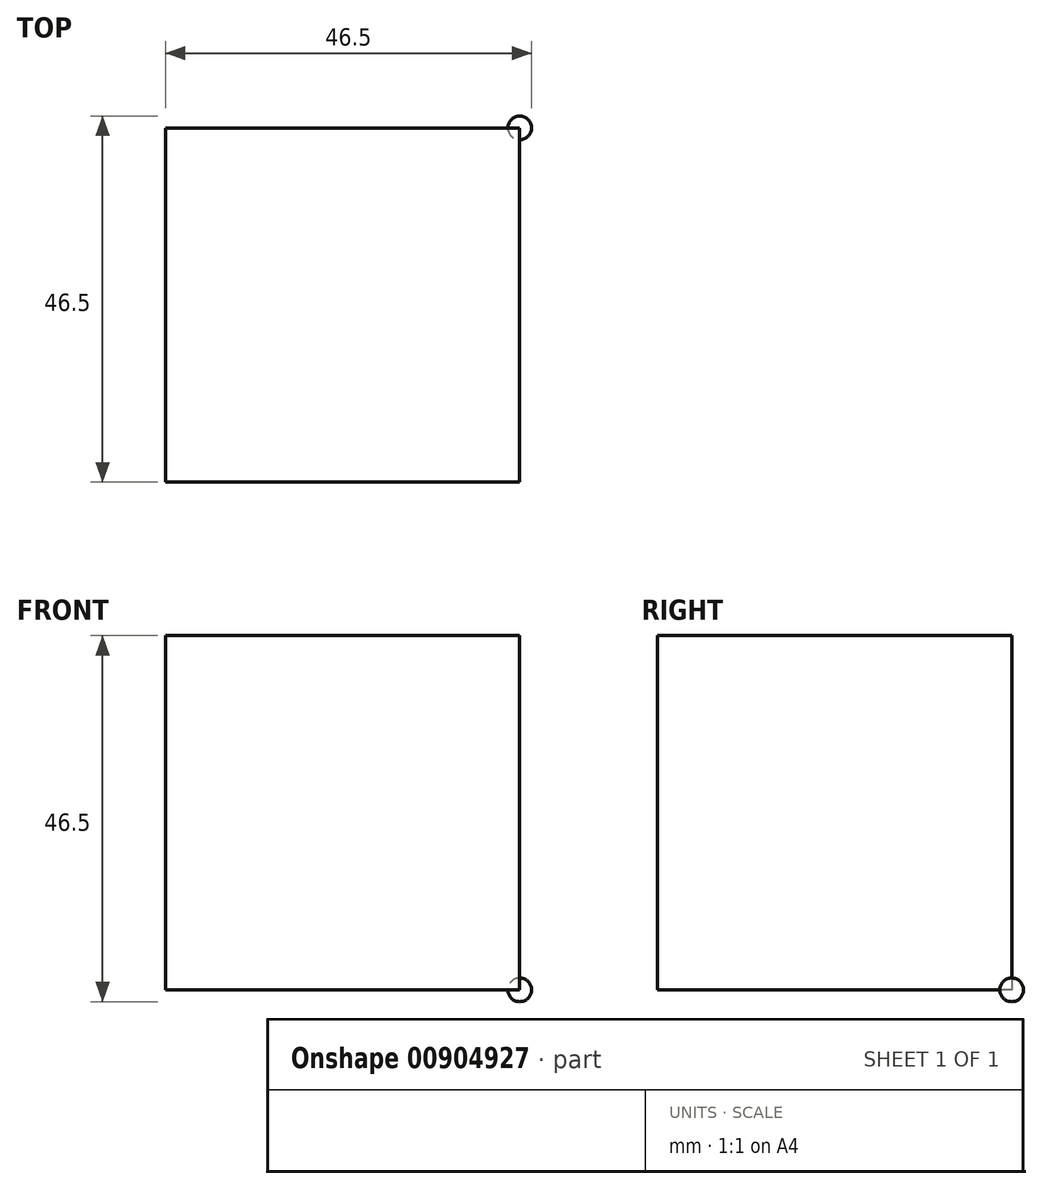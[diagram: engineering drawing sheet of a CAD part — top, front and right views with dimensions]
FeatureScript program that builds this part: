
annotation { "Feature Type Name" : "Feature", "Feature Type Description" : "" }
export const myFeature = defineFeature(function(context is Context, id is Id, definition is map)
    precondition{}
    {
        {
            var Q0;
            Q0=qCreatedBy(makeId("Top.planeOp"),FACE);
            var sketch = newSketch(context, id + "F0", { "sketchPlane" : qUnion([Q0])});
            skLineSegment(sketch, "E0.bottom", {"start": v(-22.5, 22.5) * mm, "end": v(22.5, 22.5) * mm});
            skLineSegment(sketch, "E0.top", {"start": v(-22.5, -22.5) * mm, "end": v(22.5, -22.5) * mm});
            skLineSegment(sketch, "E0.left", {"start": v(-22.5, 22.5) * mm, "end": v(-22.5, -22.5) * mm});
            skLineSegment(sketch, "E0.right", {"start": v(22.5, 22.5) * mm, "end": v(22.5, -22.5) * mm});
            skPoint(sketch, "E0.middle", {"position": v(0, 0) * mm});
            skArc(sketch, "E1", {"start": v(24, 22.5) * mm, "mid": v(22.5, 24) * mm, "end": v(21, 22.5) * mm});
            skCircle(sketch, "E2", {"center": v(22.5, -22.5) * mm, "radius": 1.5 * mm});
            skCircle(sketch, "E3", {"center": v(-22.5, 22.5) * mm, "radius": 1.5 * mm});
            skCircle(sketch, "E4", {"center": v(-22.5, -22.5) * mm, "radius": 1.5 * mm});
            skLineSegment(sketch, "E5", {"start": v(22.5, 22.5) * mm, "end": v(24, 22.5) * mm});
            skSolve(sketch);
        }
        {
            var Q0;
            {var subQ5=sQuery(id+"F0.wireOp",EDGE,"E3");var subQ13=sQuery(id+"F0.wireOp",EDGE,"E0.bottom");var subQ14=makeQuery(id+"F0.imprint","INTERSECT",VERTEX,{"derivedFrom":[subQ13,subQ5]});Q0=makeQuery(id+"F0.imprint","IMPRINT",FACE,{"disambiguationData":[TD([[makeQuery(id+"F0.imprint","IMPRINT",EDGE,{"disambiguationData":[TD([[subQ14,-1.0]])],"derivedFrom":subQ13}),-1.0]])]});}
            var Q1;
            {var subQ0=sQuery(id+"F0.wireOp",EDGE,"E0.right");var subQ1=sQuery(id+"F0.wireOp",EDGE,"E0.bottom");var subQ2=makeQuery(id+"F0.imprint","INTERSECT",VERTEX,{"derivedFrom":[subQ1,subQ0]});Q1=makeQuery(id+"F0.imprint","IMPRINT",FACE,{"disambiguationData":[TD([[makeQuery(id+"F0.imprint","IMPRINT",EDGE,{"disambiguationData":[TD([[subQ2,1.0]])],"derivedFrom":subQ1}),-1.0]])]});}
            var Q2;
            {var subQ0=sQuery(id+"F0.wireOp",EDGE,"E0.right");var subQ1=sQuery(id+"F0.wireOp",EDGE,"E0.top");var subQ2=makeQuery(id+"F0.imprint","INTERSECT",VERTEX,{"derivedFrom":[subQ1,subQ0]});Q2=makeQuery(id+"F0.imprint","IMPRINT",FACE,{"disambiguationData":[TD([[makeQuery(id+"F0.imprint","IMPRINT",EDGE,{"disambiguationData":[TD([[subQ2,1.0]])],"derivedFrom":subQ1}),1.0]])]});}
            var Q3;
            {var subQ0=sQuery(id+"F0.wireOp",EDGE,"E0.left");var subQ1=sQuery(id+"F0.wireOp",EDGE,"E0.bottom");var subQ2=makeQuery(id+"F0.imprint","INTERSECT",VERTEX,{"derivedFrom":[subQ1,subQ0]});Q3=makeQuery(id+"F0.imprint","IMPRINT",FACE,{"disambiguationData":[TD([[makeQuery(id+"F0.imprint","IMPRINT",EDGE,{"disambiguationData":[TD([[subQ2,-1.0]])],"derivedFrom":subQ1}),-1.0]])]});}
            var Q4;
            {var subQ0=sQuery(id+"F0.wireOp",EDGE,"E0.left");var subQ1=sQuery(id+"F0.wireOp",EDGE,"E0.top");var subQ2=makeQuery(id+"F0.imprint","INTERSECT",VERTEX,{"derivedFrom":[subQ1,subQ0]});Q4=makeQuery(id+"F0.imprint","IMPRINT",FACE,{"disambiguationData":[TD([[makeQuery(id+"F0.imprint","IMPRINT",EDGE,{"disambiguationData":[TD([[subQ2,-1.0]])],"derivedFrom":subQ1}),1.0]])]});}
            extrude(context, id + "F1", {"entities" : qUnion([Q0, Q1, Q2, Q3, Q4]), "depth" : 45 * mm, "offsetDistance" : 25.4 * mm});
        }
        {
            var Q0;
            {var subQ2=sQuery(id+"F0.wireOp",EDGE,"E1");Q0=makeQuery(id+"F0.imprint","IMPRINT",FACE,{"disambiguationData":[TD([[makeQuery(id+"F0.imprint","IMPRINT",EDGE,{"derivedFrom":subQ2}),1.0]])]});}
            var Q1;
            Q1=sQuery(id+"F0.wireOp",EDGE,"E5");
            revolve(context, id + "F2", {"surfaceOperationType" : NewSurfaceOperationType.NEW, "entities" : qUnion([Q0]), "axis" : qUnion([Q1]), "revolveType" : RevolveType.FULL});
        }
    });
